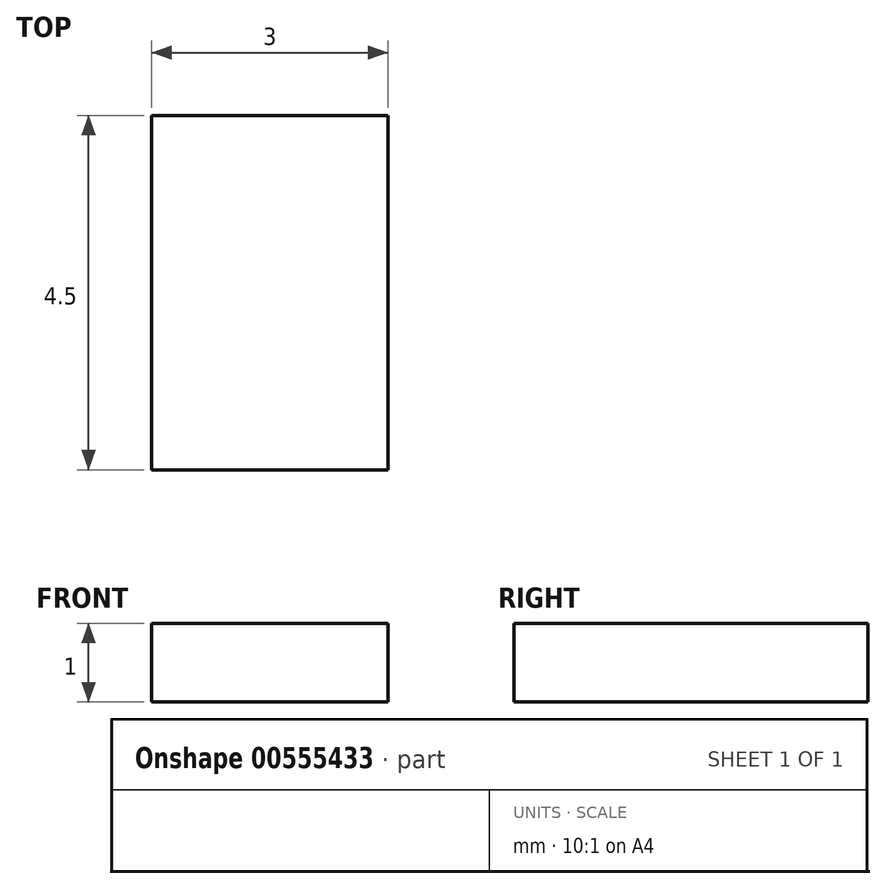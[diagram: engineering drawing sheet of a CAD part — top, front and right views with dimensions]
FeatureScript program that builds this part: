
annotation { "Feature Type Name" : "Feature", "Feature Type Description" : "" }
export const myFeature = defineFeature(function(context is Context, id is Id, definition is map)
    precondition{}
    {
        {
            var Q0;
            Q0=qCreatedBy(makeId("Top.planeOp"),FACE);
            var sketch = newSketch(context, id + "F0", { "sketchPlane" : qUnion([Q0])});
            skLineSegment(sketch, "E0.bottom", {"start": v(-1.5, 2.25) * mm, "end": v(1.5, 2.25) * mm});
            skLineSegment(sketch, "E0.top", {"start": v(-1.5, -2.25) * mm, "end": v(1.5, -2.25) * mm});
            skLineSegment(sketch, "E0.left", {"start": v(-1.5, 2.25) * mm, "end": v(-1.5, -2.25) * mm});
            skLineSegment(sketch, "E0.right", {"start": v(1.5, 2.25) * mm, "end": v(1.5, -2.25) * mm});
            skPoint(sketch, "E0.middle", {"position": v(0, 0) * mm});
            skSolve(sketch);
        }
        {
            var Q0;
            Q0 = qSketchRegion(id + "F0", true);
            extrude(context, id + "F1", {"entities" : qUnion([Q0]), "depth" : 1 * mm, "offsetDistance" : 25.4 * mm});
        }
    });
